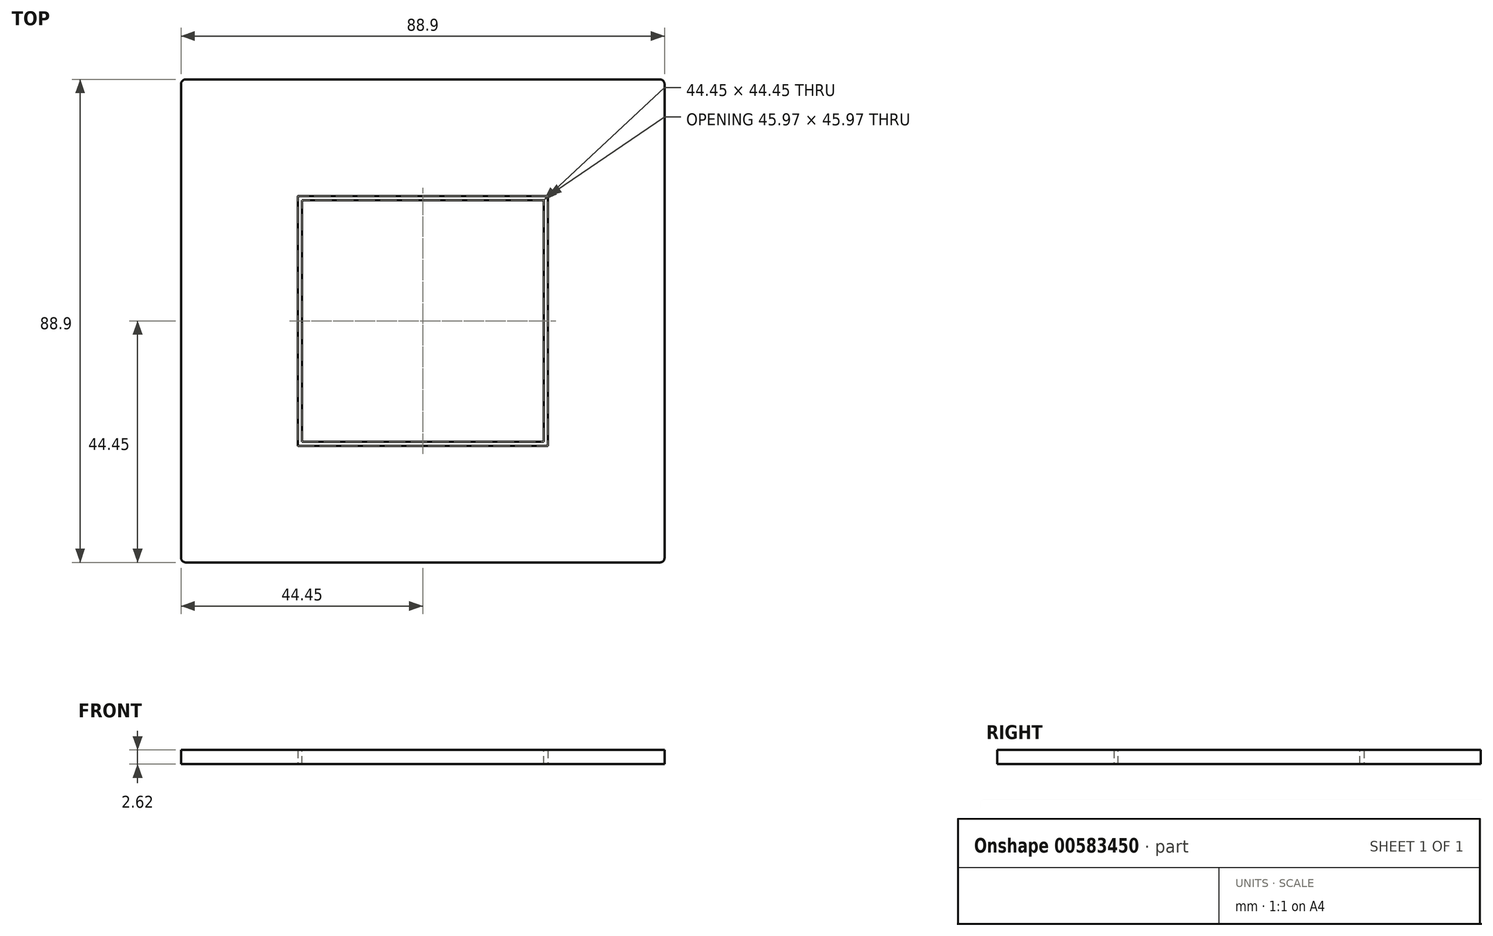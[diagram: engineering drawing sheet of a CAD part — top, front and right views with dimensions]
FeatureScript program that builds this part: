
annotation { "Feature Type Name" : "Feature", "Feature Type Description" : "" }
export const myFeature = defineFeature(function(context is Context, id is Id, definition is map)
    precondition{}
    {
        {
            assignVariable(context, id + "F0", {"name" : "Tongue", "anyValue" : 1.75});
        }
        {
            assignVariable(context, id + "F1", {"name" : "WindingWidth", "anyValue" : 3 * getVariable(context, 'Tongue') / 2});
        }
        {
            assignVariable(context, id + "F2", {"name" : "CoilForm", "anyValue" : 0.03});
        }
        {
            assignVariable(context, id + "F3", {"name" : "CoilBuild", "anyValue" : 1 * (getVariable(context, 'Tongue') / 2)});
        }
        {
            var Q0;
            Q0=qCreatedBy(makeId("Top.planeOp"),FACE);
            var sketch = newSketch(context, id + "F4", { "sketchPlane" : qUnion([Q0])});
            skLineSegment(sketch, "E0.bottom", {"start": v(22.99, 22.99) * mm, "end": v(-22.99, 22.99) * mm});
            skLineSegment(sketch, "E0.top", {"start": v(22.99, -22.99) * mm, "end": v(-22.99, -22.99) * mm});
            skLineSegment(sketch, "E0.left", {"start": v(22.99, 22.99) * mm, "end": v(22.99, -22.99) * mm});
            skLineSegment(sketch, "E0.right", {"start": v(-22.99, 22.99) * mm, "end": v(-22.99, -22.99) * mm});
            skPoint(sketch, "E0.middle", {"position": v(0, 0) * mm});
            skSolve(sketch);
        }
        {
            var Q0;
            Q0=qSketchRegion(id+"F4",true);
            extrude(context, id + "F5", {"entities" : qUnion([Q0]), "depth" : (getVariable(context, 'WindingWidth')) * mm});
        }
        {
            var Q0;
            Q0=makeQuery(id+"F5.opExtrude","CAP_FACE",FACE,{"disambiguationData":[OSD([sQuery(id+"F4.wireOp",EDGE,"E0.bottom"),sQuery(id+"F4.wireOp",EDGE,"E0.top"),sQuery(id+"F4.wireOp",EDGE,"E0.left"),sQuery(id+"F4.wireOp",EDGE,"E0.right")])],"isStart":false});
            var sketch = newSketch(context, id + "F6", { "sketchPlane" : qUnion([Q0])});
            skLineSegment(sketch, "E1.bottom", {"start": v(22.22, 22.23) * mm, "end": v(-22.23, 22.23) * mm});
            skLineSegment(sketch, "E1.top", {"start": v(22.22, -22.23) * mm, "end": v(-22.23, -22.23) * mm});
            skLineSegment(sketch, "E1.left", {"start": v(22.22, 22.23) * mm, "end": v(22.22, -22.23) * mm});
            skLineSegment(sketch, "E1.right", {"start": v(-22.23, 22.23) * mm, "end": v(-22.23, -22.23) * mm});
            skPoint(sketch, "E1.middle", {"position": v(0, 0) * mm});
            skSolve(sketch);
        }
        {
            var Q0;
            Q0=qSketchRegion(id+"F6",true);
            extrude(context, id + "F7", {"entities" : qUnion([Q0]), "operationType" : NewBodyOperationType.REMOVE, "oppositeDirection" : true, "depth" : (getVariable(context, 'WindingWidth')) * mm});
        }
        {
            var Q0;
            Q0=makeQuery(id+"F5.opExtrude","SWEPT_EDGE",EDGE,{"disambiguationData":[OSD([sQuery(id+"F4.wireOp",EDGE,"E0.bottom"),sQuery(id+"F4.wireOp",EDGE,"E0.right")])]});
            var Q1;
            Q1=makeQuery(id+"F5.opExtrude","SWEPT_EDGE",EDGE,{"disambiguationData":[OSD([sQuery(id+"F4.wireOp",EDGE,"E0.bottom"),sQuery(id+"F4.wireOp",EDGE,"E0.left")])]});
            var Q2;
            Q2=makeQuery(id+"F5.opExtrude","SWEPT_EDGE",EDGE,{"disambiguationData":[OSD([sQuery(id+"F4.wireOp",EDGE,"E0.top"),sQuery(id+"F4.wireOp",EDGE,"E0.right")])]});
            var Q3;
            Q3=makeQuery(id+"F5.opExtrude","SWEPT_EDGE",EDGE,{"disambiguationData":[OSD([sQuery(id+"F4.wireOp",EDGE,"E0.top"),sQuery(id+"F4.wireOp",EDGE,"E0.left")])]});
            fillet(context, id + "F8", {"entities" : qUnion([Q0, Q1, Q2, Q3]), "radius" : (getVariable(context, 'CoilForm')) * mm, "tangentPropagation" : true, "allowEdgeOverflow" : false});
        }
        {
            var Q0;
            Q0=makeQuery(id+"F5.opExtrude","CAP_FACE",FACE,{"disambiguationData":[OSD([sQuery(id+"F4.wireOp",EDGE,"E0.bottom"),sQuery(id+"F4.wireOp",EDGE,"E0.top"),sQuery(id+"F4.wireOp",EDGE,"E0.left"),sQuery(id+"F4.wireOp",EDGE,"E0.right")])],"isStart":false});
            var sketch = newSketch(context, id + "F9", { "sketchPlane" : qUnion([Q0])});
            skLineSegment(sketch, "E2.bottom", {"start": v(-44.45, 44.45) * mm, "end": v(44.45, 44.45) * mm});
            skLineSegment(sketch, "E2.top", {"start": v(-44.45, -44.45) * mm, "end": v(44.45, -44.45) * mm});
            skLineSegment(sketch, "E2.left", {"start": v(-44.45, 44.45) * mm, "end": v(-44.45, -44.45) * mm});
            skLineSegment(sketch, "E2.right", {"start": v(44.45, 44.45) * mm, "end": v(44.45, -44.45) * mm});
            skPoint(sketch, "E2.middle", {"position": v(0, 0) * mm});
            skLineSegment(sketch, "E3.bottom", {"start": v(-22.99, 22.99) * mm, "end": v(22.99, 22.99) * mm});
            skLineSegment(sketch, "E3.top", {"start": v(-22.99, -22.99) * mm, "end": v(22.99, -22.99) * mm});
            skLineSegment(sketch, "E3.left", {"start": v(-22.99, 22.99) * mm, "end": v(-22.99, -22.99) * mm});
            skLineSegment(sketch, "E3.right", {"start": v(22.99, 22.99) * mm, "end": v(22.99, -22.99) * mm});
            skSolve(sketch);
        }
        {
            var Q0;
            Q0=makeQuery(id+"F9.imprint","IMPRINT",FACE,{"disambiguationData":[TD([[makeQuery(id+"F9.imprint","IMPRINT",EDGE,{"derivedFrom":sQuery(id+"F9.wireOp",EDGE,"E2.bottom")}),-1.0]])]});
            extrude(context, id + "F10", {"entities" : qUnion([Q0]), "oppositeDirection" : true, "depth" : (getVariable(context, 'WindingWidth')) * mm});
        }
        {
            var Q0;
            Q0=makeQuery(id+"F10.opExtrude","SWEPT_EDGE",EDGE,{"disambiguationData":[OSD([sQuery(id+"F9.wireOp",EDGE,"E2.bottom"),sQuery(id+"F9.wireOp",EDGE,"E2.left")])]});
            var Q1;
            Q1=makeQuery(id+"F10.opExtrude","SWEPT_EDGE",EDGE,{"disambiguationData":[OSD([sQuery(id+"F9.wireOp",EDGE,"E2.top"),sQuery(id+"F9.wireOp",EDGE,"E2.left")])]});
            var Q2;
            Q2=makeQuery(id+"F10.opExtrude","SWEPT_EDGE",EDGE,{"disambiguationData":[OSD([sQuery(id+"F9.wireOp",EDGE,"E2.top"),sQuery(id+"F9.wireOp",EDGE,"E2.right")])]});
            var Q3;
            Q3=makeQuery(id+"F10.opExtrude","SWEPT_EDGE",EDGE,{"disambiguationData":[OSD([sQuery(id+"F9.wireOp",EDGE,"E2.bottom"),sQuery(id+"F9.wireOp",EDGE,"E2.right")])]});
            fillet(context, id + "F11", {"entities" : qUnion([Q0, Q1, Q2, Q3]), "radius" : (getVariable(context, 'CoilBuild')) * mm, "tangentPropagation" : true, "allowEdgeOverflow" : false});
        }
        {
            var Q0;
            Q0=makeQuery(id+"F10.opExtrude","SWEPT_EDGE",EDGE,{"disambiguationData":[OSD([sQuery(id+"F9.wireOp",EDGE,"E3.bottom"),sQuery(id+"F9.wireOp",EDGE,"E3.left")])]});
            var Q1;
            Q1=makeQuery(id+"F10.opExtrude","SWEPT_EDGE",EDGE,{"disambiguationData":[OSD([sQuery(id+"F9.wireOp",EDGE,"E3.bottom"),sQuery(id+"F9.wireOp",EDGE,"E3.right")])]});
            var Q2;
            Q2=makeQuery(id+"F10.opExtrude","SWEPT_EDGE",EDGE,{"disambiguationData":[OSD([sQuery(id+"F9.wireOp",EDGE,"E3.top"),sQuery(id+"F9.wireOp",EDGE,"E3.right")])]});
            var Q3;
            Q3=makeQuery(id+"F10.opExtrude","SWEPT_EDGE",EDGE,{"disambiguationData":[OSD([sQuery(id+"F9.wireOp",EDGE,"E3.top"),sQuery(id+"F9.wireOp",EDGE,"E3.left")])]});
            fillet(context, id + "F12", {"entities" : qUnion([Q0, Q1, Q2, Q3]), "radius" : (getVariable(context, 'CoilForm')) * mm, "tangentPropagation" : true, "allowEdgeOverflow" : false});
        }
    });
